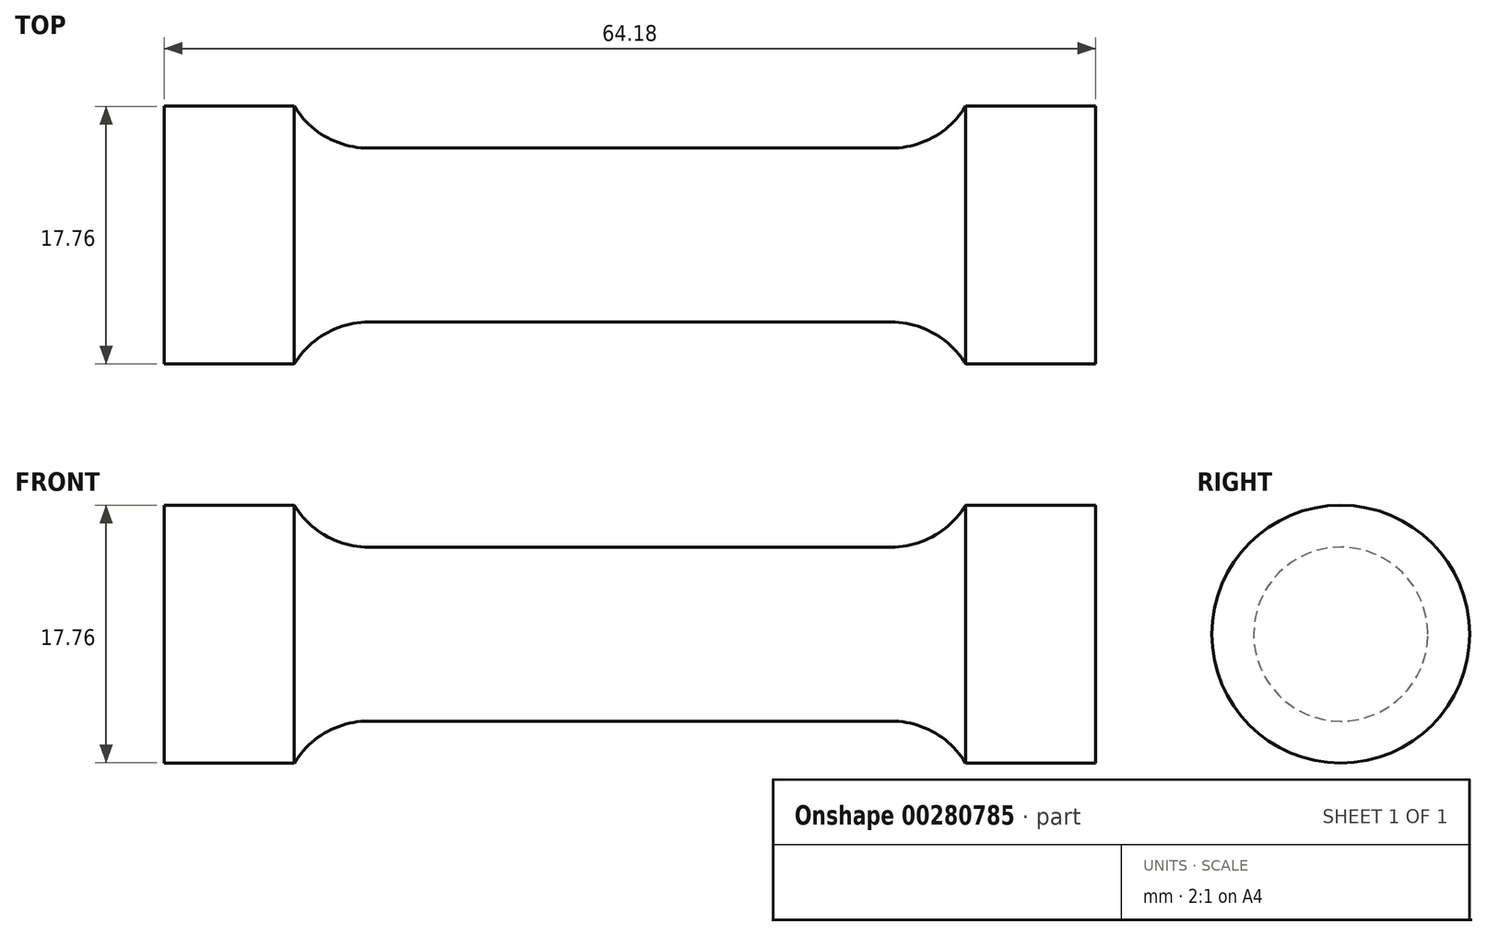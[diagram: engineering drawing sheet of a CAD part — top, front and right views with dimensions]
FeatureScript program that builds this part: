
annotation { "Feature Type Name" : "Feature", "Feature Type Description" : "" }
export const myFeature = defineFeature(function(context is Context, id is Id, definition is map)
    precondition{}
    {
        {
            var Q0;
            Q0=qCreatedBy(makeId("Front.planeOp"),FACE);
            var sketch = newSketch(context, id + "F0", { "sketchPlane" : qUnion([Q0])});
            skLineSegment(sketch, "E0", {"start": v(0, 6) * mm, "end": v(18, 6) * mm});
            skArc(sketch, "E1", {"start": v(18, 6) * mm, "mid": v(20.94, 6.77) * mm, "end": v(23.13, 8.88) * mm});
            skLineSegment(sketch, "E2", {"start": v(23.13, 8.88) * mm, "end": v(32.09, 8.88) * mm});
            skLineSegment(sketch, "E3", {"start": v(32.09, 8.88) * mm, "end": v(32.09, 0) * mm});
            skLineSegment(sketch, "E4.MirrorCS", {"start": v(0, 6) * mm, "end": v(-18, 6) * mm});
            skLineSegment(sketch, "E5.MirrorCS", {"start": v(-32.09, 8.88) * mm, "end": v(-32.09, 0) * mm});
            skLineSegment(sketch, "E6.MirrorCS", {"start": v(-23.13, 8.88) * mm, "end": v(-32.09, 8.88) * mm});
            skArc(sketch, "E7.MirrorCS", {"start": v(-18, 6) * mm, "mid": v(-20.94, 6.77) * mm, "end": v(-23.13, 8.88) * mm});
            skLineSegment(sketch, "E8", {"start": v(-32.09, 0) * mm, "end": v(32.09, 0) * mm});
            skSolve(sketch);
        }
        {
            var Q0;
            Q0 = qSketchRegion(id + "F0", true);
            var Q1;
            Q1=sQuery(id+"F0.wireOp",EDGE,"E8");
            revolve(context, id + "F1", {"entities" : qUnion([Q0]), "axis" : qUnion([Q1]), "revolveType" : RevolveType.FULL});
        }
    });
